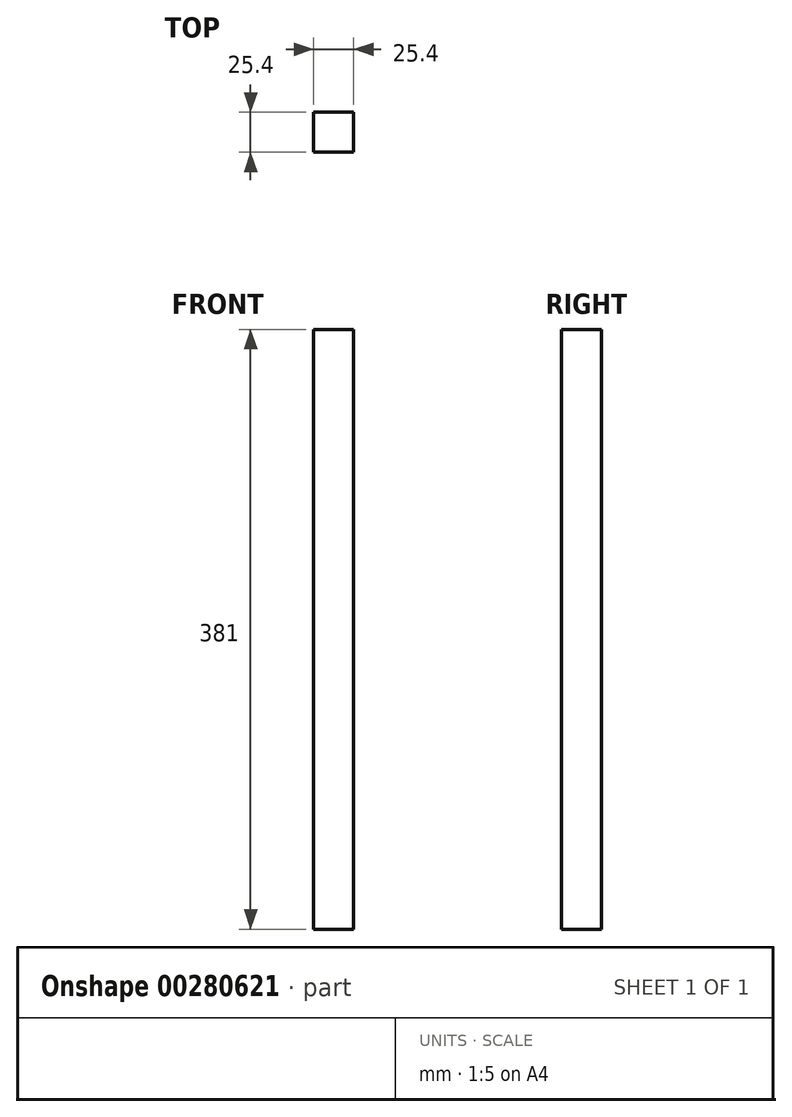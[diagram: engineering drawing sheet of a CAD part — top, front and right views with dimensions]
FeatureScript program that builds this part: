
annotation { "Feature Type Name" : "Feature", "Feature Type Description" : "" }
export const myFeature = defineFeature(function(context is Context, id is Id, definition is map)
    precondition{}
    {
        {
            var Q0;
            Q0=qCreatedBy(makeId("Top.planeOp"),FACE);
            var sketch = newSketch(context, id + "F0", { "sketchPlane" : qUnion([Q0])});
            skLineSegment(sketch, "E0.bottom", {"start": v(-9.63, 19.14) * mm, "end": v(15.77, 19.14) * mm});
            skLineSegment(sketch, "E0.top", {"start": v(-9.63, -6.26) * mm, "end": v(15.77, -6.26) * mm});
            skLineSegment(sketch, "E0.left", {"start": v(-9.63, 19.14) * mm, "end": v(-9.63, -6.26) * mm});
            skLineSegment(sketch, "E0.right", {"start": v(15.77, 19.14) * mm, "end": v(15.77, -6.26) * mm});
            skSolve(sketch);
        }
        {
            var Q0;
            Q0 = qSketchRegion(id + "F0", true);
            var Q1;
            Q1=makeQuery(id+"F0.imprint","IMPRINT",FACE,{"disambiguationData":[TD([[makeQuery(id+"F0.imprint","IMPRINT",EDGE,{"derivedFrom":sQuery(id+"F0.wireOp",EDGE,"E0.bottom")}),-1.0]])]});
            extrude(context, id + "F1", {"entities" : qUnion([Q0, Q1]), "depth" : 381 * mm});
        }
    });
